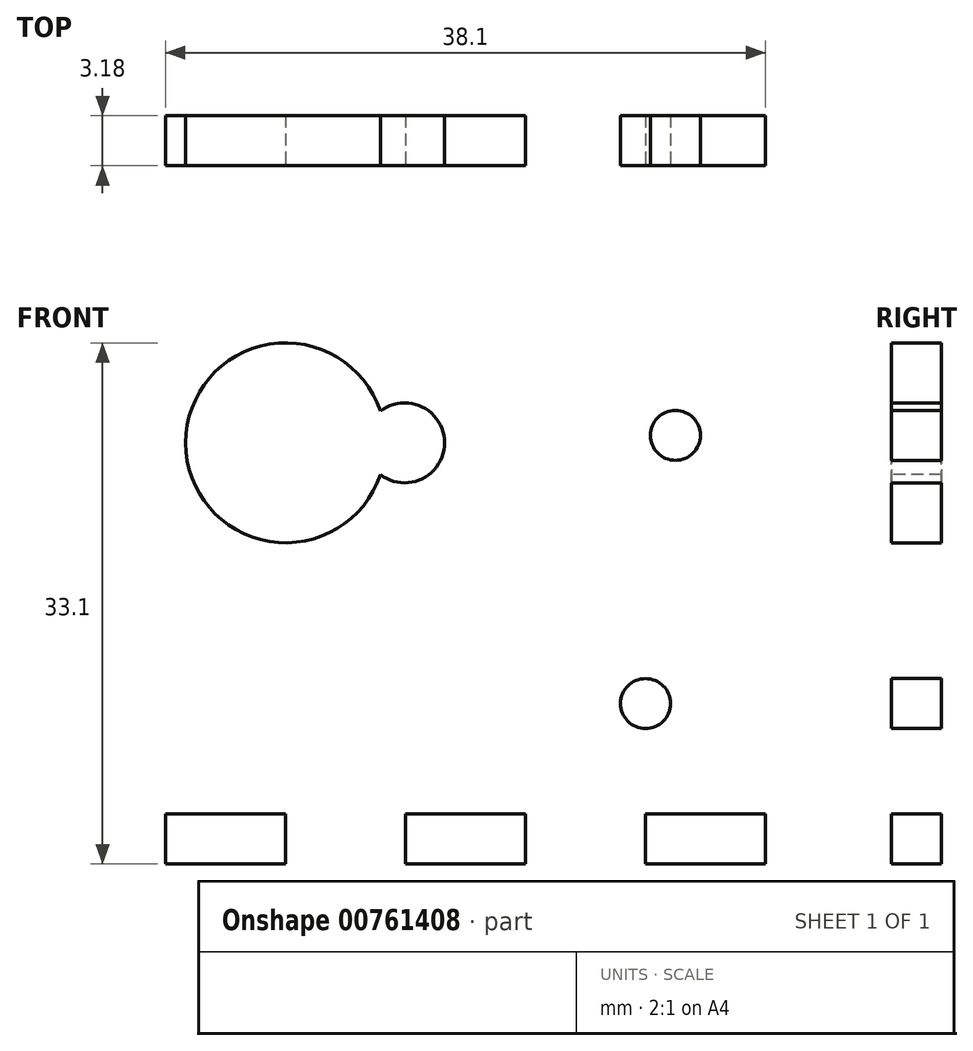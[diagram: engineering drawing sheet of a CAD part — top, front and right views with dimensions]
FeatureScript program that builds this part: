
annotation { "Feature Type Name" : "Feature", "Feature Type Description" : "" }
export const myFeature = defineFeature(function(context is Context, id is Id, definition is map)
    precondition{}
    {
        {
            var Q0;
            Q0=qCreatedBy(makeId("Front.planeOp"),FACE);
            var sketch = newSketch(context, id + "F0", { "sketchPlane" : qUnion([Q0])});
            skPoint(sketch, "E0.middle", {"position": v(0, 0) * mm});
            skLineSegment(sketch, "E1.bottom", {"start": v(-25.26, 16.76) * mm, "end": v(12.84, 16.76) * mm});
            skLineSegment(sketch, "E1.top", {"start": v(-25.26, -21.34) * mm, "end": v(12.84, -21.34) * mm});
            skLineSegment(sketch, "E1.left", {"start": v(-25.26, 16.76) * mm, "end": v(-25.26, -21.34) * mm});
            skLineSegment(sketch, "E1.right", {"start": v(12.84, 16.76) * mm, "end": v(12.84, -21.34) * mm});
            skSolve(sketch);
        }
        {
            var Q0;
            Q0=qSketchRegion(id+"F0",true);
            extrude(context, id + "F1", {"entities" : qUnion([Q0]), "depth" : 3.17 * mm, "offsetDistance" : 25.4 * mm});
        }
        {
            var Q0;
            Q0=makeQuery(id+"F1.opExtrude","CAP_FACE",FACE,{"disambiguationData":[OSD([sQuery(id+"F0.wireOp",EDGE,"E1.bottom"),sQuery(id+"F0.wireOp",EDGE,"E1.top"),sQuery(id+"F0.wireOp",EDGE,"E1.left"),sQuery(id+"F0.wireOp",EDGE,"E1.right")])],"isStart":false});
            var sketch = newSketch(context, id + "F2", { "sketchPlane" : qUnion([Q0])});
            skLineSegment(sketch, "E2.MirrorCS", {"start": v(-2.4, -21.34) * mm, "end": v(-10.02, -21.34) * mm});
            skLineSegment(sketch, "E3.MirrorCS", {"start": v(-17.64, -21.34) * mm, "end": v(-25.26, -21.34) * mm});
            skLineSegment(sketch, "E4.MirrorCS", {"start": v(12.84, -18.16) * mm, "end": v(12.84, -21.34) * mm});
            skLineSegment(sketch, "E5.MirrorCS", {"start": v(12.84, -21.34) * mm, "end": v(5.22, -21.34) * mm});
            skLineSegment(sketch, "E6.MirrorCS", {"start": v(5.22, -18.16) * mm, "end": v(5.22, -21.34) * mm});
            skCircle(sketch, "E7.MirrorC", {"center": v(7.13, 5.88) * mm, "radius": 1.59 * mm});
            skArc(sketch, "E8.MirrorCS", {"start": v(-11.61, 7.43) * mm, "mid": v(-7.53, 5.4) * mm, "end": v(-11.61, 3.39) * mm});
            skArc(sketch, "E9.MirrorCS", {"start": v(-11.61, 3.39) * mm, "mid": v(-23.99, 5.4) * mm, "end": v(-11.61, 7.43) * mm});
            skLineSegment(sketch, "E10.MirrorCS", {"start": v(12.84, 16.76) * mm, "end": v(12.84, -21.34) * mm});
            skLineSegment(sketch, "E11.MirrorCS", {"start": v(12.84, -21.34) * mm, "end": v(-25.26, -21.34) * mm});
            skLineSegment(sketch, "E12.MirrorCS", {"start": v(12.84, 16.76) * mm, "end": v(-25.26, 16.76) * mm});
            skLineSegment(sketch, "E13.MirrorCS", {"start": v(-10.02, -18.16) * mm, "end": v(-10.02, -21.34) * mm});
            skLineSegment(sketch, "E14.MirrorCS", {"start": v(-2.4, -18.16) * mm, "end": v(-2.4, -21.34) * mm});
            skLineSegment(sketch, "E15.MirrorCS", {"start": v(-10.02, -18.16) * mm, "end": v(-17.64, -18.16) * mm});
            skLineSegment(sketch, "E16.MirrorCS", {"start": v(-17.64, -18.16) * mm, "end": v(-25.26, -18.16) * mm});
            skLineSegment(sketch, "E17.MirrorCS", {"start": v(-17.64, -18.16) * mm, "end": v(-17.64, -21.34) * mm});
            skCircle(sketch, "E18.MirrorC", {"center": v(5.22, -11.16) * mm, "radius": 1.59 * mm});
            skLineSegment(sketch, "E19.MirrorCS", {"start": v(12.84, -18.16) * mm, "end": v(5.22, -18.16) * mm});
            skLineSegment(sketch, "E20.MirrorCS", {"start": v(5.22, -18.16) * mm, "end": v(-2.4, -18.16) * mm});
            skLineSegment(sketch, "E21.MirrorCS", {"start": v(-2.4, -18.16) * mm, "end": v(-10.02, -18.16) * mm});
            skLineSegment(sketch, "E22", {"start": v(-25.26, 16.76) * mm, "end": v(-25.26, -21.34) * mm});
            skSolve(sketch);
        }
        {
            var Q0;
            {var subQ0=sQuery(id+"F2.wireOp",EDGE,"E13.MirrorCS");Q0=makeQuery(id+"F2.imprint","IMPRINT",FACE,{"disambiguationData":[TD([[makeQuery(id+"F2.imprint","IMPRINT",EDGE,{"derivedFrom":subQ0}),-1.0]])]});}
            var Q1;
            {var subQ0=sQuery(id+"F2.wireOp",EDGE,"E6.MirrorCS");Q1=makeQuery(id+"F2.imprint","IMPRINT",FACE,{"disambiguationData":[TD([[makeQuery(id+"F2.imprint","IMPRINT",EDGE,{"derivedFrom":subQ0}),-1.0]])]});}
            var Q2;
            Q2=makeQuery(id+"F2.imprint","IMPRINT",FACE,{"disambiguationData":[TD([[makeQuery(id+"F2.imprint","IMPRINT",EDGE,{"derivedFrom":sQuery(id+"F2.wireOp",EDGE,"E8.MirrorCS")}),-1.0]])]});
            var Q3;
            Q3=makeQuery(id+"F2.imprint","IMPRINT",FACE,{"disambiguationData":[TD([[makeQuery(id+"F2.imprint","IMPRINT",EDGE,{"derivedFrom":sQuery(id+"F2.wireOp",EDGE,"E7.MirrorC")}),-1.0]])]});
            var Q4;
            Q4=makeQuery(id+"F2.imprint","IMPRINT",FACE,{"disambiguationData":[TD([[makeQuery(id+"F2.imprint","IMPRINT",EDGE,{"derivedFrom":sQuery(id+"F2.wireOp",EDGE,"E18.MirrorC")}),-1.0]])]});
            extrude(context, id + "F3", {"entities" : qUnion([Q0, Q1, Q2, Q3, Q4]), "operationType" : NewBodyOperationType.REMOVE, "oppositeDirection" : true, "depth" : 3.17 * mm, "offsetDistance" : 25.4 * mm});
        }
    });
